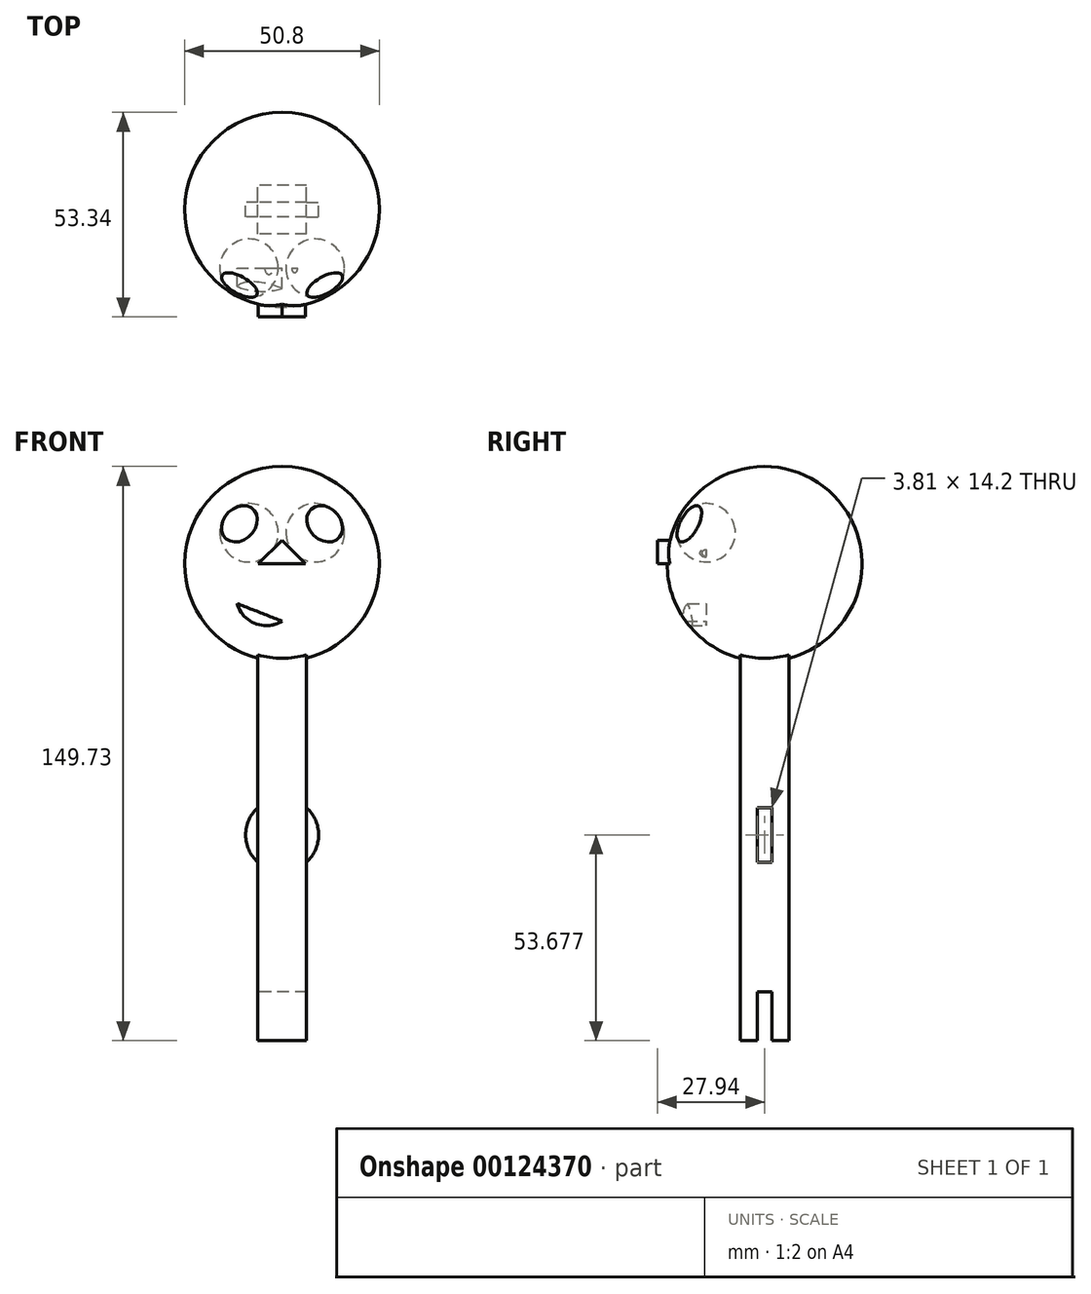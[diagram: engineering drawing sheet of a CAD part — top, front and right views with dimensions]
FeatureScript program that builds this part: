
annotation { "Feature Type Name" : "Feature", "Feature Type Description" : "" }
export const myFeature = defineFeature(function(context is Context, id is Id, definition is map)
    precondition{}
    {
        {
            var Q0;
            Q0=qCreatedBy(makeId("Front.planeOp"),FACE);
            var sketch = newSketch(context, id + "F0", { "sketchPlane" : qUnion([Q0])});
            skLineSegment(sketch, "E0", {"start": v(0, 0) * mm, "end": v(-25.4, 0) * mm});
            skLineSegment(sketch, "E1", {"start": v(0, 0) * mm, "end": v(25.4, 0) * mm});
            skArc(sketch, "E2", {"start": v(25.4, 0) * mm, "mid": v(17.96, 17.96) * mm, "end": v(0, 25.4) * mm});
            skArc(sketch, "E3", {"start": v(-25.4, 0) * mm, "mid": v(-17.96, 17.96) * mm, "end": v(0, 25.4) * mm});
            skSolve(sketch);
        }
        {
            var Q0;
            Q0=makeQuery(id+"F0.imprint","IMPRINT",FACE,{"disambiguationData":[TD([[makeQuery(id+"F0.imprint","IMPRINT",EDGE,{"derivedFrom":sQuery(id+"F0.wireOp",EDGE,"E0")}),-1.0]])]});
            var Q1;
            Q1=sQuery(id+"F0.wireOp",EDGE,"E0");
            revolve(context, id + "F1", {"entities" : qUnion([Q0]), "axis" : qUnion([Q1]), "revolveType" : RevolveType.FULL});
        }
        {
            var Q0;
            Q0=qCreatedBy(makeId("Top.planeOp"),FACE);
            var sketch = newSketch(context, id + "F2", { "sketchPlane" : qUnion([Q0])});
            skLineSegment(sketch, "E4", {"start": v(0, 0) * mm, "end": v(0, -15.24) * mm, "construction": true});
            skSolve(sketch);
        }
        {
            var Q0;
            Q0=qCreatedBy(makeId("Front.planeOp"),FACE);
            var Q1;
            Q1=sQuery(id+"F2.wireOp",VERTEX,"E4.end");
            cPlane(context, id + "F3", {"entities" : qUnion([Q0, Q1]), "cplaneType" : CPlaneType.PLANE_POINT, "offset" : 25.4 * mm, "width" : 152.4 * mm, "height" : 152.4 * mm});
        }
        {
            var Q0;
            Q0=qCreatedBy(id+"F3.planeOp",FACE);
            var sketch = newSketch(context, id + "F4", { "sketchPlane" : qUnion([Q0])});
            skLineSegment(sketch, "E5", {"start": v(16.26, 8.13) * mm, "end": v(1.02, 8.13) * mm});
            skArc(sketch, "E6", {"start": v(16.26, 8.13) * mm, "mid": v(8.64, 15.75) * mm, "end": v(1.02, 8.13) * mm});
            skLineSegment(sketch, "E7", {"start": v(8.64, 8.13) * mm, "end": v(8.64, 15.75) * mm, "construction": true});
            skLineSegment(sketch, "E8", {"start": v(0, 25.3) * mm, "end": v(0, 0) * mm, "construction": true});
            skLineSegment(sketch, "E9", {"start": v(0, 0) * mm, "end": v(0, 25.3) * mm, "construction": true});
            skLineSegment(sketch, "E10", {"start": v(1.02, 8.13) * mm, "end": v(0, 8.13) * mm, "construction": true});
            skSolve(sketch);
        }
        {
            var Q0;
            Q0 = qSketchRegion(id + "F4", true);
            var Q1;
            Q1=sQuery(id+"F4.wireOp",EDGE,"E5");
            revolve(context, id + "F5", {"operationType" : NewBodyOperationType.REMOVE, "entities" : qUnion([Q0]), "axis" : qUnion([Q1]), "revolveType" : RevolveType.FULL});
        }
        {
            var Q0;
            Q0=makeQuery(id+"F1.opRevolve","SWEPT_BODY",BODY,{"disambiguationData":[OSD([sQuery(id+"F0.wireOp",EDGE,"E0"),sQuery(id+"F0.wireOp",EDGE,"E1"),sQuery(id+"F0.wireOp",EDGE,"E2"),sQuery(id+"F0.wireOp",EDGE,"E3")])]});
            var Q1;
            Q1=qCreatedBy(makeId("Right.planeOp"),FACE);
            mirror(context, id + "F6", {"operationType" : NewBodyOperationType.INTERSECT, "entities" : qUnion([Q0]), "mirrorPlane" : qUnion([Q1])});
        }
        {
            var Q0;
            Q0=qCreatedBy(id+"F3.planeOp",FACE);
            var sketch = newSketch(context, id + "F7", { "sketchPlane" : qUnion([Q0])});
            skLineSegment(sketch, "E11", {"start": v(-6.28, 0) * mm, "end": v(0, 6.16) * mm});
            skLineSegment(sketch, "E12", {"start": v(0, 6.16) * mm, "end": v(6.06, 0) * mm});
            skLineSegment(sketch, "E13", {"start": v(6.06, 0) * mm, "end": v(-6.28, 0) * mm});
            skSolve(sketch);
        }
        {
            var Q0;
            Q0 = qSketchRegion(id + "F7", true);
            extrude(context, id + "F8", {"entities" : qUnion([Q0]), "operationType" : NewBodyOperationType.ADD, "depth" : 12.7 * mm});
        }
        {
            var Q0;
            Q0=qCreatedBy(id+"F3.planeOp",FACE);
            var sketch = newSketch(context, id + "F9", { "sketchPlane" : qUnion([Q0])});
            skArc(sketch, "E14", {"start": v(-11.73, -10.34) * mm, "mid": v(-7.01, -15.57) * mm, "end": v(0, -14.92) * mm});
            skLineSegment(sketch, "E15", {"start": v(-11.73, -10.34) * mm, "end": v(0, -14.92) * mm});
            skSolve(sketch);
        }
        {
            var Q0;
            Q0 = qSketchRegion(id + "F9", true);
            extrude(context, id + "F10", {"entities" : qUnion([Q0]), "operationType" : NewBodyOperationType.REMOVE, "depth" : 38.1 * mm});
        }
        {
            var Q0;
            Q0=qCreatedBy(makeId("Right.planeOp"),FACE);
            var sketch = newSketch(context, id + "F11", { "sketchPlane" : qUnion([Q0])});
            skLineSegment(sketch, "E16.bottom", {"start": v(-6.35, 2.67) * mm, "end": v(6.35, 2.67) * mm});
            skLineSegment(sketch, "E16.top", {"start": v(-6.35, -124.33) * mm, "end": v(6.35, -124.33) * mm});
            skLineSegment(sketch, "E16.left", {"start": v(-6.35, 2.67) * mm, "end": v(-6.35, -124.33) * mm});
            skLineSegment(sketch, "E16.right", {"start": v(6.35, 2.67) * mm, "end": v(6.35, -124.33) * mm});
            skLineSegment(sketch, "E17", {"start": v(0, 2.67) * mm, "end": v(0, 0) * mm, "construction": true});
            skSolve(sketch);
        }
        {
            var Q0;
            Q0 = qSketchRegion(id + "F11", true);
            extrude(context, id + "F12", {"entities" : qUnion([Q0]), "operationType" : NewBodyOperationType.ADD, "endBound" : BoundingType.SYMMETRIC, "depth" : 12.7 * mm});
        }
        {
            var Q0;
            Q0=makeQuery(id+"F12.opExtrude","CAP_FACE",FACE,{"disambiguationData":[OSD([sQuery(id+"F11.wireOp",EDGE,"E16.bottom"),sQuery(id+"F11.wireOp",EDGE,"E16.top"),sQuery(id+"F11.wireOp",EDGE,"E16.left"),sQuery(id+"F11.wireOp",EDGE,"E16.right")])],"isStart":false});
            var sketch = newSketch(context, id + "F13", { "sketchPlane" : qUnion([Q0])});
            skLineSegment(sketch, "E18.bottom", {"start": v(-1.9, -124.33) * mm, "end": v(1.9, -124.33) * mm});
            skLineSegment(sketch, "E18.top", {"start": v(-1.9, -111.63) * mm, "end": v(1.9, -111.63) * mm});
            skLineSegment(sketch, "E18.left", {"start": v(-1.9, -124.33) * mm, "end": v(-1.9, -111.63) * mm});
            skLineSegment(sketch, "E18.right", {"start": v(1.9, -124.33) * mm, "end": v(1.9, -111.63) * mm});
            skLineSegment(sketch, "E19", {"start": v(0, 0) * mm, "end": v(0, -111.63) * mm, "construction": true});
            skSolve(sketch);
        }
        {
            var Q0;
            Q0 = qSketchRegion(id + "F13", true);
            extrude(context, id + "F14", {"entities" : qUnion([Q0]), "operationType" : NewBodyOperationType.REMOVE, "endBound" : BoundingType.SYMMETRIC, "depth" : 25.4 * mm});
        }
        {
            var Q0;
            Q0=qCreatedBy(makeId("Front.planeOp"),FACE);
            var sketch = newSketch(context, id + "F15", { "sketchPlane" : qUnion([Q0])});
            skCircle(sketch, "E20", {"center": v(0, -70.65) * mm, "radius": 9.53 * mm});
            skSolve(sketch);
        }
        {
            var Q0;
            Q0 = qSketchRegion(id + "F15", true);
            extrude(context, id + "F16", {"entities" : qUnion([Q0]), "operationType" : NewBodyOperationType.ADD, "endBound" : BoundingType.SYMMETRIC, "depth" : 3.8 * mm});
        }
    });
